# Revit family: E_Cable Tray Support_MEPcontent_OBO Bettermann_Bracket AWSS FT
name_source: partatom
category: Cable Tray Fittings
revit_build: Autodesk Revit MEP 2015 (Build: 20140606_1530(x64)
units: mm (PartAtom-declared; Revit-internal decimal feet)

## types (1)
- AWSS 61 FT
    Article Description = Wall Bracket
    Article Type = AWSS 61 FT
    Depth = 400 mm  [stored 1.31234 ft]
    Description = Wall Bracket
    EMCS Version = 2.0
    ETIM Article Class = EC000022
    Family Version = 10.14
    Front Height = 111.67 mm
    GTIN = 4012196340514
    Gray = Color RGB 189-187-185
    Height = 335 mm
    Height 1 = 335 mm  [stored 1.09908 ft]
    IFCExportAs = IfcCableCarrierFittingType
    IFCExportType = NOTDEFINED
    MEPcontent Class = CABLE_TRAY_SUPPORT
    Manufacturer = OBO BETTERMANN
    Manufacturer Art. No. = 6417922
    Manufacturer URL = http://catalog4.obo-bettermann.com
    Model = AWSS 61 FT
    Product Line = OBO BETTERMANN CableTrays
    Revit Version = 2015
    URL = www.stabiplan.com
    Width = 610 mm
    Width 1 = 610 mm  [stored 2.00131 ft]

note: [stored X ft] marks values corroborated as IEEE doubles in the binary element streams (Revit-internal decimal feet)

## geometry (parser evidence)
native form markers: Blend x4, Sweep x3
no freeform markers — native parametric forms only
